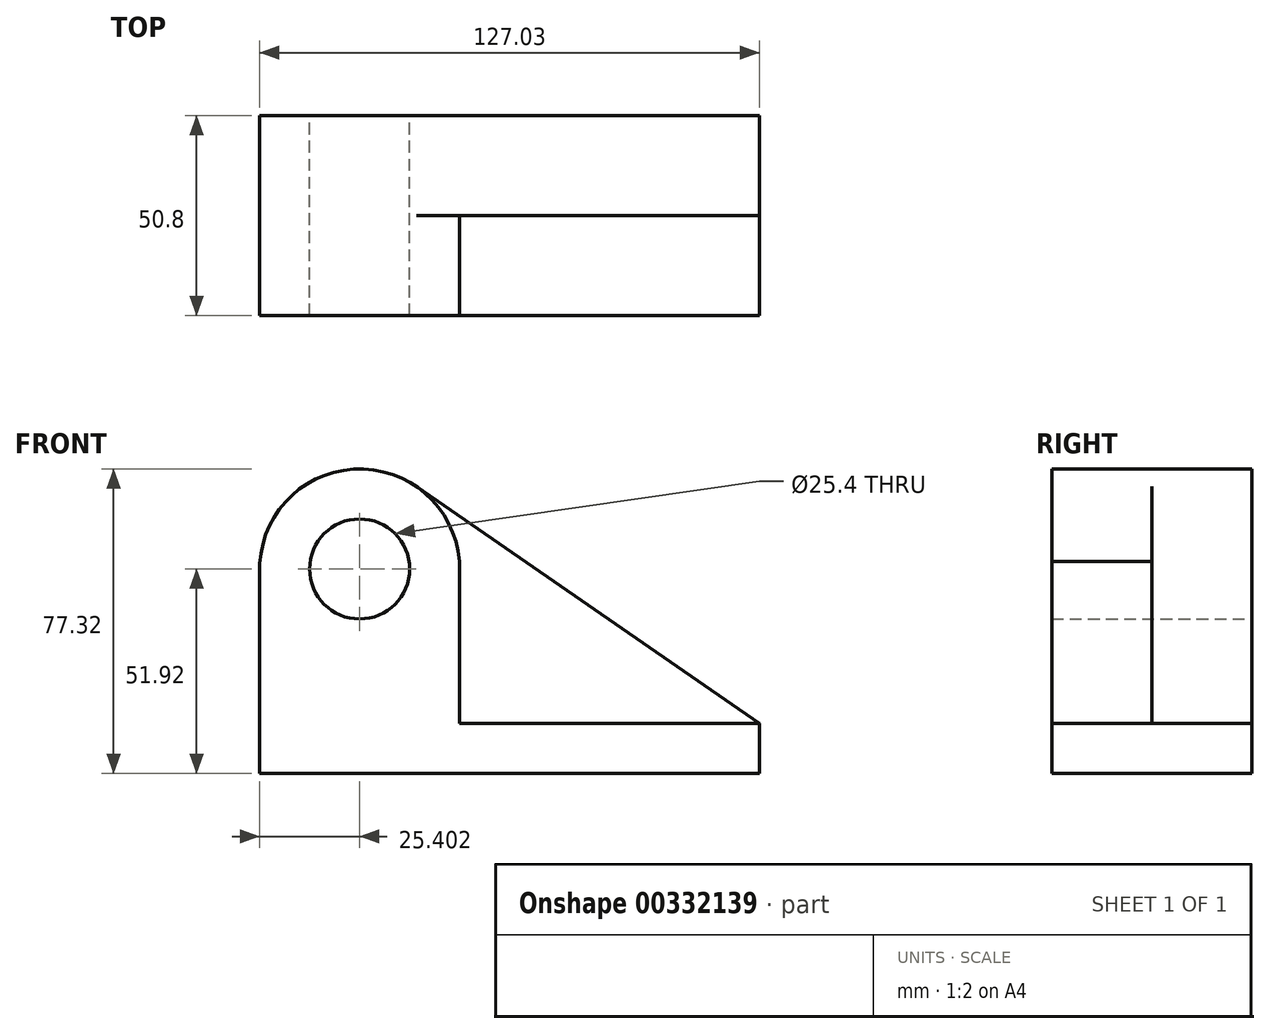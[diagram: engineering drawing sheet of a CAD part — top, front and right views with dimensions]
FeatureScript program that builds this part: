
annotation { "Feature Type Name" : "Feature", "Feature Type Description" : "" }
export const myFeature = defineFeature(function(context is Context, id is Id, definition is map)
    precondition{}
    {
        {
            var Q0;
            Q0=qCreatedBy(makeId("Front.planeOp"),FACE);
            var sketch = newSketch(context, id + "F0", { "sketchPlane" : qUnion([Q0])});
            skCircle(sketch, "E0", {"center": v(-47.66, 46.27) * mm, "radius": 12.7 * mm});
            skArc(sketch, "E1", {"start": v(-33.24, 67.18) * mm, "mid": v(-59.96, 68.5) * mm, "end": v(-73.03, 45.15) * mm});
            skLineSegment(sketch, "E2", {"start": v(-73.03, 45.15) * mm, "end": v(-73.03, -5.65) * mm});
            skLineSegment(sketch, "E3", {"start": v(-73.03, -5.65) * mm, "end": v(53.97, -5.65) * mm});
            skLineSegment(sketch, "E4", {"start": v(53.97, -5.65) * mm, "end": v(53.97, 7.05) * mm});
            skLineSegment(sketch, "E5", {"start": v(53.97, 7.05) * mm, "end": v(-33.24, 67.18) * mm});
            skSolve(sketch);
        }
        {
            var Q0;
            {var subQ0=sQuery(id+"F0.wireOp",EDGE,"E2");Q0=makeQuery(id+"F0.imprint","IMPRINT",FACE,{"disambiguationData":[TD([[makeQuery(id+"F0.imprint","IMPRINT",EDGE,{"derivedFrom":subQ0}),1.0]])]});}
            extrude(context, id + "F1", {"entities" : qUnion([Q0]), "depth" : 25.4 * mm});
        }
        {
            var Q0;
            Q0=makeQuery(id+"F1.opExtrude","CAP_FACE",FACE,{"disambiguationData":[OSD([sQuery(id+"F0.wireOp",EDGE,"E0"),sQuery(id+"F0.wireOp",EDGE,"E1"),sQuery(id+"F0.wireOp",EDGE,"E2"),sQuery(id+"F0.wireOp",EDGE,"E3"),sQuery(id+"F0.wireOp",EDGE,"E4"),sQuery(id+"F0.wireOp",EDGE,"E5")])],"isStart":false});
            var sketch = newSketch(context, id + "F2", { "sketchPlane" : qUnion([Q0])});
            skCircle(sketch, "E6", {"center": v(-47.66, 46.27) * mm, "radius": 12.7 * mm});
            skArc(sketch, "E7", {"start": v(-22.33, 44.3) * mm, "mid": v(-47.23, 71.67) * mm, "end": v(-73.03, 45.15) * mm});
            skLineSegment(sketch, "E8.bottom", {"start": v(53.97, 7.05) * mm, "end": v(-22.33, 7.05) * mm});
            skLineSegment(sketch, "E8.top", {"start": v(53.97, -5.65) * mm, "end": v(-73.03, -5.65) * mm});
            skLineSegment(sketch, "E8.left", {"start": v(53.97, 7.05) * mm, "end": v(53.97, -5.65) * mm});
            skLineSegment(sketch, "E8.right", {"start": v(-73.03, 7.05) * mm, "end": v(-73.03, -5.65) * mm});
            skLineSegment(sketch, "E9", {"start": v(-22.33, 48.23) * mm, "end": v(-22.33, 7.05) * mm});
            skLineSegment(sketch, "E10", {"start": v(-73.03, 46.27) * mm, "end": v(-73.03, 7.05) * mm});
            skSolve(sketch);
        }
        {
            var Q0;
            Q0=makeQuery(id+"F2.imprint","IMPRINT",FACE,{"disambiguationData":[TD([[makeQuery(id+"F2.imprint","IMPRINT",EDGE,{"derivedFrom":sQuery(id+"F2.wireOp",EDGE,"E6")}),-1.0]])]});
            extrude(context, id + "F3", {"entities" : qUnion([Q0]), "operationType" : NewBodyOperationType.ADD, "depth" : 25.4 * mm});
        }
    });
